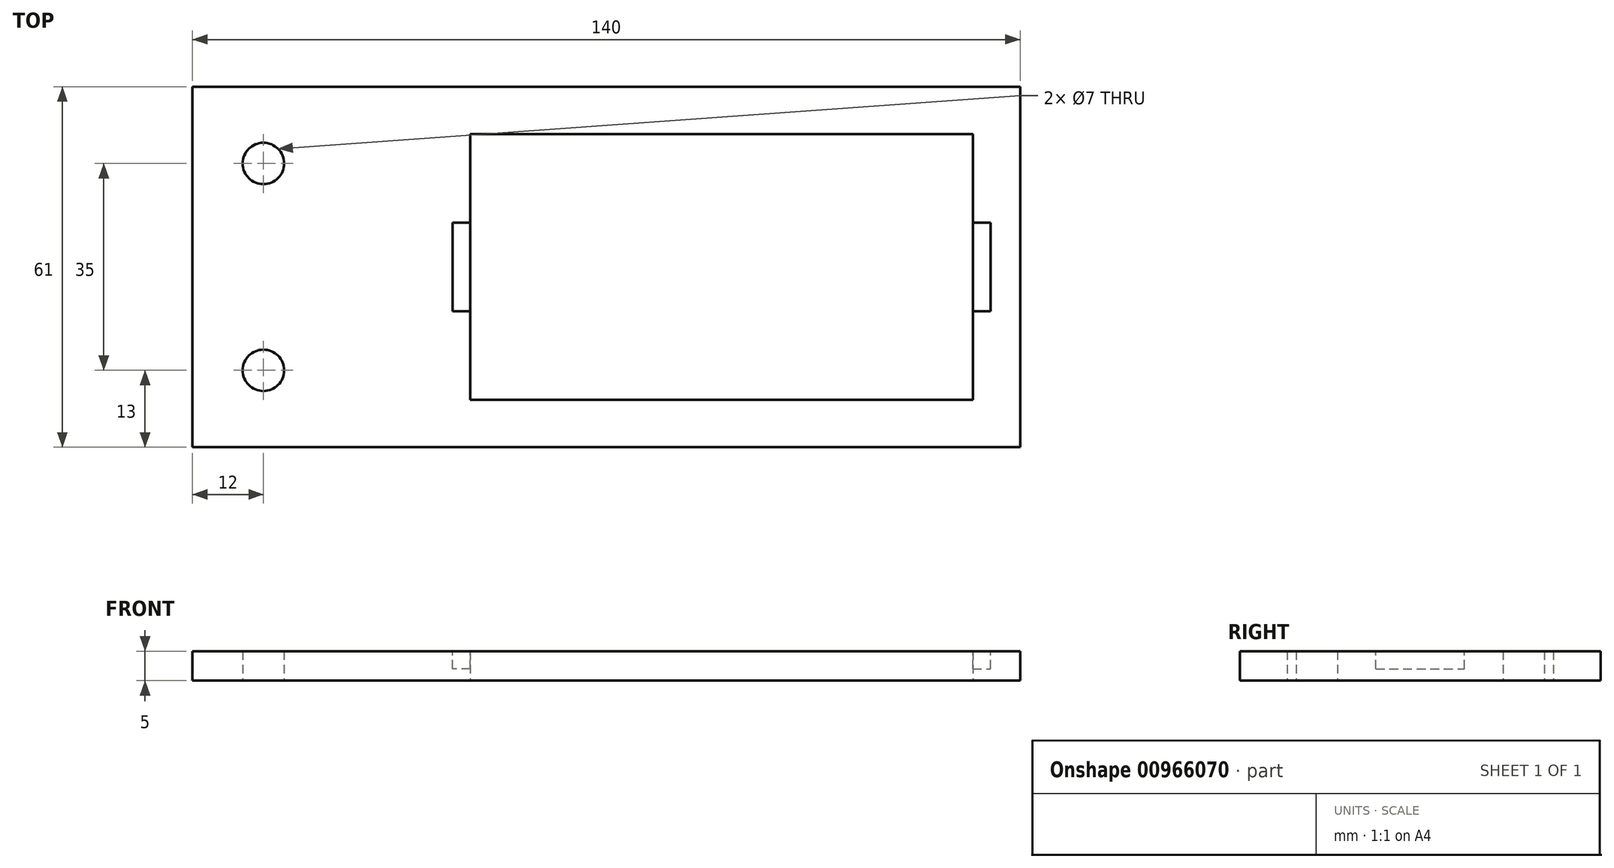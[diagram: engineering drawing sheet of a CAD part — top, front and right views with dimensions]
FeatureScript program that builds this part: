
annotation { "Feature Type Name" : "Feature", "Feature Type Description" : "" }
export const myFeature = defineFeature(function(context is Context, id is Id, definition is map)
    precondition{}
    {
        {
            var Q0;
            Q0=qCreatedBy(makeId("Top.planeOp"),FACE);
            var sketch = newSketch(context, id + "F0", { "sketchPlane" : qUnion([Q0])});
            skLineSegment(sketch, "E0.bottom", {"start": v(0, 0) * mm, "end": v(85, 0) * mm});
            skLineSegment(sketch, "E0.top", {"start": v(0, 45) * mm, "end": v(85, 45) * mm});
            skLineSegment(sketch, "E0.left", {"start": v(0, 0) * mm, "end": v(0, 45) * mm});
            skLineSegment(sketch, "E0.right", {"start": v(85, 0) * mm, "end": v(85, 45) * mm});
            skLineSegment(sketch, "E1.bottom", {"start": v(93, 53) * mm, "end": v(-47, 53) * mm});
            skLineSegment(sketch, "E1.top", {"start": v(93, -8) * mm, "end": v(-47, -8) * mm});
            skLineSegment(sketch, "E1.left", {"start": v(93, 53) * mm, "end": v(93, -8) * mm});
            skLineSegment(sketch, "E1.right", {"start": v(-47, 53) * mm, "end": v(-47, -8) * mm});
            skCircle(sketch, "E2", {"center": v(-35, 40) * mm, "radius": 3.5 * mm});
            skCircle(sketch, "E3", {"center": v(-35, 5) * mm, "radius": 3.5 * mm});
            skSolve(sketch);
        }
        {
            var Q0;
            Q0 = qSketchRegion(id + "F0", true);
            extrude(context, id + "F1", {"entities" : qUnion([Q0]), "depth" : 5 * mm, "offsetDistance" : 25 * mm});
        }
        {
            var Q0;
            Q0=makeQuery(id+"F1.opExtrude","CAP_FACE",FACE,{"disambiguationData":[OSD([sQuery(id+"F0.wireOp",EDGE,"E0.bottom"),sQuery(id+"F0.wireOp",EDGE,"E0.top"),sQuery(id+"F0.wireOp",EDGE,"E0.left"),sQuery(id+"F0.wireOp",EDGE,"E0.right"),sQuery(id+"F0.wireOp",EDGE,"E1.bottom"),sQuery(id+"F0.wireOp",EDGE,"E1.top"),sQuery(id+"F0.wireOp",EDGE,"E1.left"),sQuery(id+"F0.wireOp",EDGE,"E1.right"),sQuery(id+"F0.wireOp",EDGE,"E2"),sQuery(id+"F0.wireOp",EDGE,"E3")])],"isStart":false});
            var sketch = newSketch(context, id + "F2", { "sketchPlane" : qUnion([Q0])});
            skLineSegment(sketch, "E4.bottom", {"start": v(0, 30) * mm, "end": v(-3, 30) * mm});
            skLineSegment(sketch, "E4.top", {"start": v(0, 15) * mm, "end": v(-3, 15) * mm});
            skLineSegment(sketch, "E4.left", {"start": v(0, 30) * mm, "end": v(0, 15) * mm});
            skLineSegment(sketch, "E4.right", {"start": v(-3, 30) * mm, "end": v(-3, 15) * mm});
            skLineSegment(sketch, "E5.bottom", {"start": v(85, 30) * mm, "end": v(88, 30) * mm});
            skLineSegment(sketch, "E5.top", {"start": v(85, 15) * mm, "end": v(88, 15) * mm});
            skLineSegment(sketch, "E5.left", {"start": v(85, 30) * mm, "end": v(85, 15) * mm});
            skLineSegment(sketch, "E5.right", {"start": v(88, 30) * mm, "end": v(88, 15) * mm});
            skSolve(sketch);
        }
        {
            var Q0;
            Q0 = qSketchRegion(id + "F2", true);
            extrude(context, id + "F3", {"entities" : qUnion([Q0]), "operationType" : NewBodyOperationType.REMOVE, "oppositeDirection" : true, "depth" : 3 * mm, "offsetDistance" : 25 * mm});
        }
    });
